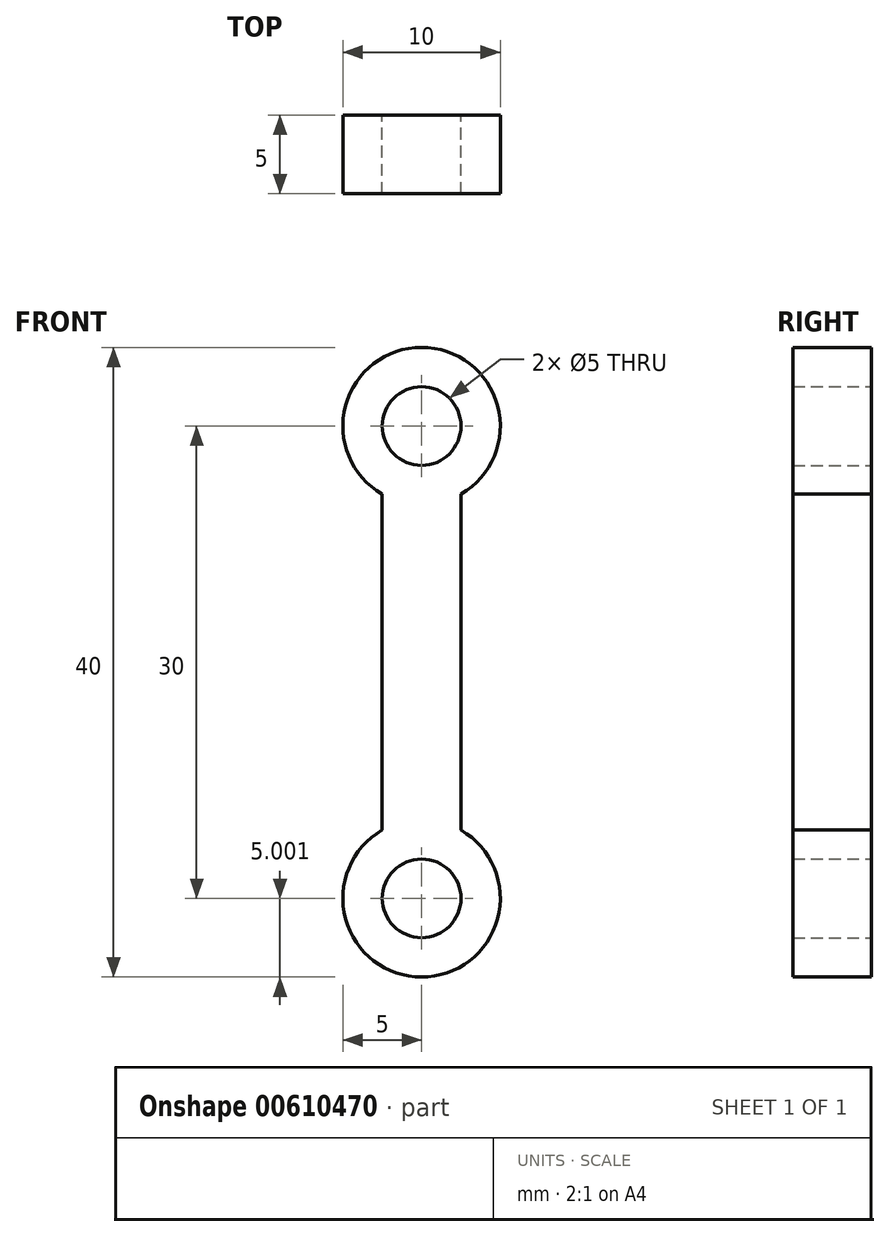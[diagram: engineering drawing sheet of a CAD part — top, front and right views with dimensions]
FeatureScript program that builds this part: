
annotation { "Feature Type Name" : "Feature", "Feature Type Description" : "" }
export const myFeature = defineFeature(function(context is Context, id is Id, definition is map)
    precondition{}
    {
        {
            var Q0;
            Q0=qCreatedBy(makeId("Front.planeOp"),FACE);
            var sketch = newSketch(context, id + "F0", { "sketchPlane" : qUnion([Q0])});
            skCircle(sketch, "E0", {"center": v(0, 13.74) * mm, "radius": 2.5 * mm});
            skCircle(sketch, "E1", {"center": v(0, -16.26) * mm, "radius": 2.5 * mm});
            skLineSegment(sketch, "E2", {"start": v(-2.5, -16.26) * mm, "end": v(-2.5, 13.74) * mm});
            skLineSegment(sketch, "E3", {"start": v(2.5, 13.7) * mm, "end": v(2.5, -16.23) * mm});
            skCircle(sketch, "E4", {"center": v(0, 13.74) * mm, "radius": 5 * mm});
            skCircle(sketch, "E5", {"center": v(0, -16.26) * mm, "radius": 5 * mm});
            skSolve(sketch);
        }
        {
            var Q0;
            Q0 = qSketchRegion(id + "F0", true);
            extrude(context, id + "F1", {"entities" : qUnion([Q0]), "depth" : 5 * mm, "offsetDistance" : 25 * mm});
        }
    });
